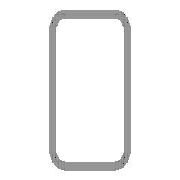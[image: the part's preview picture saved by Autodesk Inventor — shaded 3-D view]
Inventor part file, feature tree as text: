
AUTODESK INVENTOR PART (.ipt)
format: ipt  version: 2025.3 (Build 293356030, 356C)  size: 150,016 bytes
history: native  units: mm (DEFAULTED — no unit token found)
features: other x4, plane x3, split x2, sketch x1
ambient origin geometry x8: Origin, YZ Plane, XZ Plane, XY Plane, X Axis, Y Axis, Z Axis, Center Point
bodies: Solid1 (feature_tree), Body (feature_tree)
feature tree (10):
  parser-record x1  (decoder bookkeeping rows leaked as tree rows — omitted from the tree; the rows remain in map.json)
  other  "Driven Length"
  other  "Start Plane"
  other  "End Plane"
  plane  "Work Plane4"
  split  "Split1"
  plane  "Work Plane5"
  split  "Split2"
  sketch  "Sketch3"  dims[d3=3151.269837mm d4=0.0mm d7=4.0mm d9=20.0mm d11=40.0mm d12=2.0mm d13=0.0mm d14=3151.269837mm d15=10.0mm d16=20.0mm d17=90.0deg d18=3151.269837mm]
  plane  "Work Plane3"
